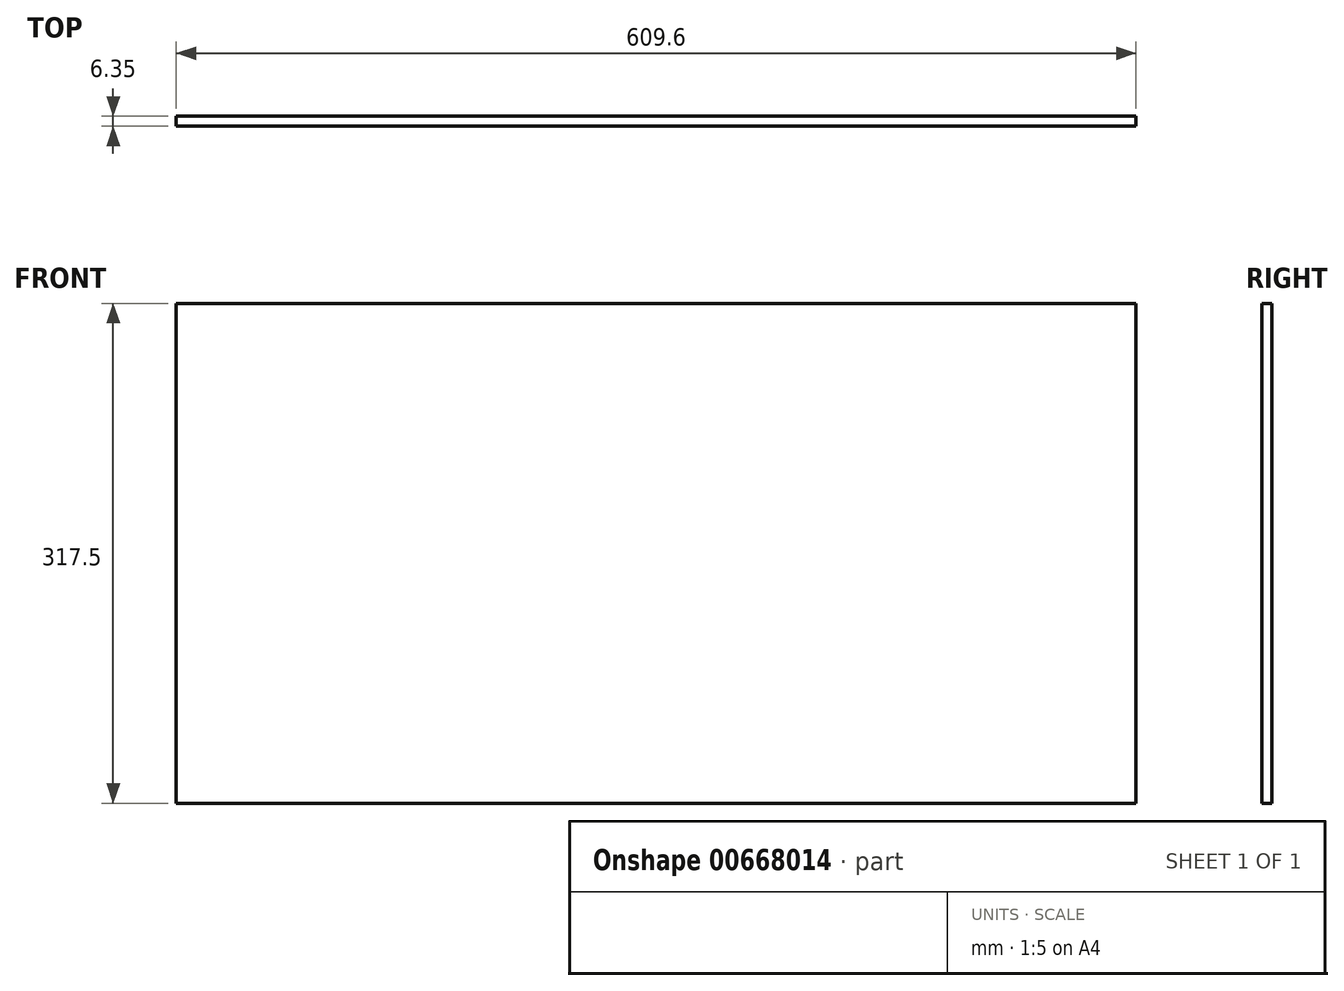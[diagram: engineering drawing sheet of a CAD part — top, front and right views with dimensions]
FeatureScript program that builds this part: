
annotation { "Feature Type Name" : "Feature", "Feature Type Description" : "" }
export const myFeature = defineFeature(function(context is Context, id is Id, definition is map)
    precondition{}
    {
        {
            var Q0;
            Q0=qCreatedBy(makeId("Front.planeOp"),FACE);
            var sketch = newSketch(context, id + "F0", { "sketchPlane" : qUnion([Q0])});
            skLineSegment(sketch, "E0.bottom", {"start": v(306.66, 158.75) * mm, "end": v(-302.94, 158.75) * mm});
            skLineSegment(sketch, "E0.top", {"start": v(306.66, -158.75) * mm, "end": v(-302.94, -158.75) * mm});
            skLineSegment(sketch, "E0.left", {"start": v(306.66, 158.75) * mm, "end": v(306.66, -158.75) * mm});
            skLineSegment(sketch, "E0.right", {"start": v(-302.94, 158.75) * mm, "end": v(-302.94, -158.75) * mm});
            skPoint(sketch, "E0.middle", {"position": v(1.86, 0) * mm});
            skSolve(sketch);
        }
        {
            var Q0;
            Q0=makeQuery(id+"F0.imprint","IMPRINT",FACE,{"disambiguationData":[TD([[makeQuery(id+"F0.imprint","IMPRINT",EDGE,{"derivedFrom":sQuery(id+"F0.wireOp",EDGE,"E0.bottom")}),1.0]])]});
            extrude(context, id + "F1", {"entities" : qUnion([Q0]), "depth" : 6.35 * mm, "offsetDistance" : 25.4 * mm});
        }
    });
